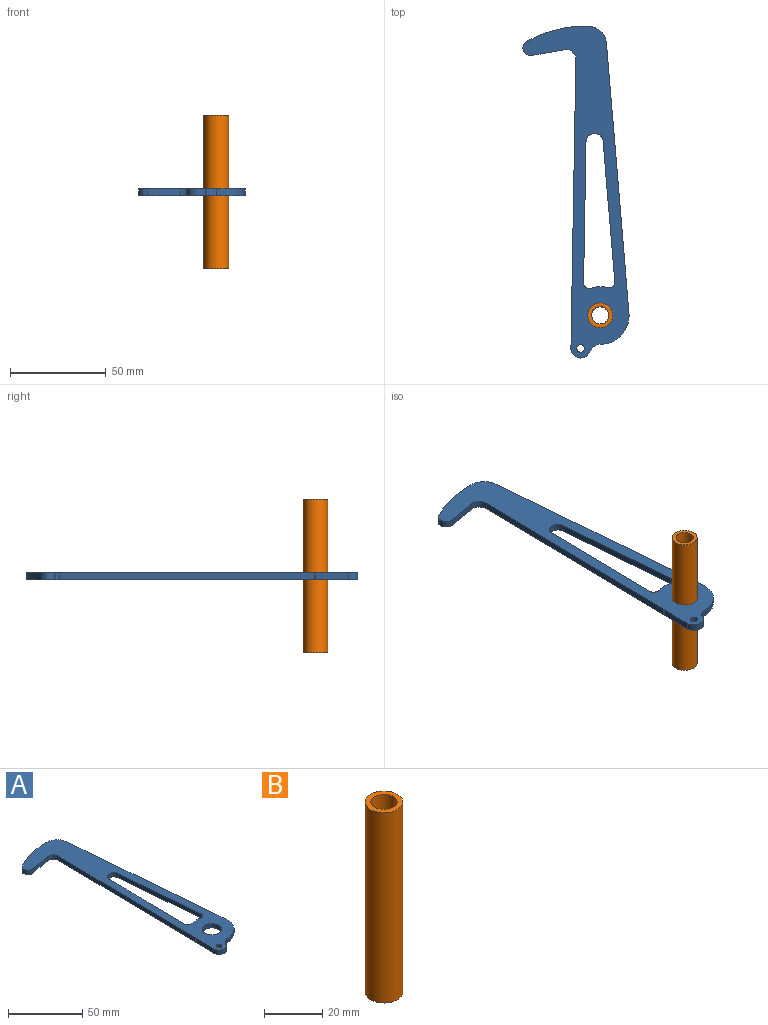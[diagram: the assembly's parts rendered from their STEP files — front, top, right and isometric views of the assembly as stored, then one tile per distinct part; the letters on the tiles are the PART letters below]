
ASSEMBLY  parts=2 mates=1
PART A: 23 faces, bbox 55.3x172.9x3.5 mm
  f0: plane 72.78x6.08mm, normal (-1,-0.08,0), area 255.6mm2, adj f15,f16,f17,f21
  f1: cylinder r=15mm len=8.56mm, axis (0,0,-1), area 30.4mm2, adj f16,f17,f21,f22
  f2: plane 73.02x3.5mm, normal (1,-0.02,0), area 255.6mm2, adj f15,f16,f17,f22
  f3: cylinder r=15mm len=3.5mm, axis (0,0,-1), area 1.7mm2, adj f4,f16,f17,f18
  f4: plane 17.06x3.5mm, normal (-1,0.02,0), area 59.7mm2, adj f3,f5,f16,f17
  f5: cylinder r=5mm len=9.72mm, axis (0,0,-1), area 49.4mm2, adj f4,f6,f16,f17
  f6: cylinder r=6.71mm len=5.57mm, axis (0,0,-1), area 24.7mm2, adj f5,f7,f16,f17
  f7: cylinder r=15mm len=16.25mm, axis (0,0,-1), area 86.8mm2, adj f6,f8,f16,f17
  f8: plane 140.37x11.73mm, normal (1,0.08,0), area 493mm2, adj f7,f16,f17,f20
  f9: cylinder r=63.38mm len=31.66mm, axis (0,0,-1), area 115.6mm2, adj f10,f16,f17,f20
  f10: cylinder r=3.95mm len=7.4mm, axis (0,0,-1), area 38.8mm2, adj f9,f11,f16,f17
  f11: plane 17.09x3.5mm, normal (0.17,-0.98,0), area 60.7mm2, adj f10,f16,f17,f19
  f12: cylinder r=6.5mm len=13mm, axis (0,0,-1), area 142.9mm2, adj f16,f17
  f13: cylinder r=2mm len=4mm, axis (0,0,-1), area 44mm2, adj f16,f17
  f14: plane 132.9x3.5mm, normal (-1,0.02,0), area 465.2mm2, adj f16,f17,f18,f19
  f15: cylinder r=4.47mm len=8.93mm, axis (0,0,-1), area 49.1mm2, adj f0,f2,f16,f17
  f16: plane 172.94x55.3mm, normal (0,0,1), area 2986.3mm2, adj f0,f1,f2,f3,f4,f5,f6,f7
  f17: plane 172.94x55.3mm, normal (0,0,-1), area 2986.3mm2, adj f0,f1,f2,f3,f4,f5,f6,f7
  f18: cylinder r=5mm len=3.5mm, axis (0,0,-1), area 0.3mm2, adj f3,f14,f16,f17
  f19: cylinder r=5mm len=5.87mm, axis (0,0,1), area 30.8mm2, adj f11,f14,f16,f17
  f20: cylinder r=10mm len=9.83mm, axis (0,0,-1), area 51.6mm2, adj f8,f9,f16,f17
  f21: cylinder r=3mm len=3.76mm, axis (0,0,-1), area 20.1mm2, adj f0,f1,f16,f17
  f22: cylinder r=3mm len=3.95mm, axis (0,0,-1), area 20.1mm2, adj f1,f2,f16,f17
PART B: 4 faces, bbox 13x13x80 mm
  f0: cylinder r=4.5mm len=80mm, axis (0,0,-1), area 2261.9mm2, adj f2,f3
  f1: cylinder r=6.5mm len=80mm, axis (0,0,-1), area 3267.3mm2, adj f2,f3
  f2: plane 13x13mm, normal (0,0,1), area 69.1mm2, adj f0,f1
  f3: plane 13x13mm, normal (0,0,-1), area 69.1mm2, adj f0,f1
PLACE A t=(17.81,20.81,14.36)mm
PLACE B t=(17.81,20.81,14.48)mm
MATE cylindrical A.f1 <-> B.f0  axis (0,0,1) through (17.81,20.81,17.86)mm
